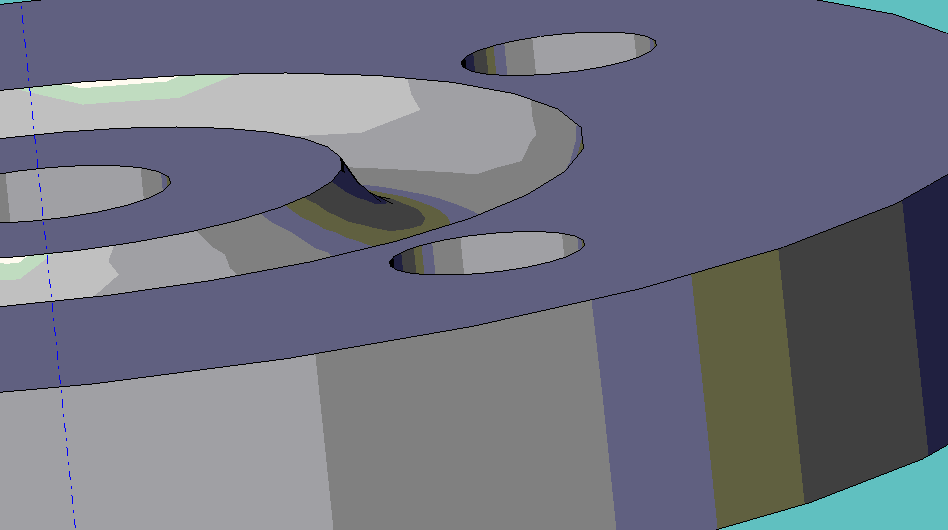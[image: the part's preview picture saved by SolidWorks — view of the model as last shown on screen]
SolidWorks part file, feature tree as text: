
SOLIDWORKS PART (.sldprt)
format: sldprt  version: not decoded by parser v0  size: 194,560 bytes
history: native  units: mm
features: sketch x4, cut_extrude x2, material x1, extrude x1, cut_revolve x1 (+12 scaffold rows collapsed)
feature tree (21):
  scaffold x12  (default folders/planes/origin — collapsed)
  material  "Material <not specified>"
  sketch  "Sketch1"  dims[D1=~12.69413mm]
  sketch  "Sketch3"  dims[D1=1.0033mm]
  extrude  "Extrude1"  Depth=3.175mm
  cut_revolve  "Cut-Revolve1"  Angle=360deg
  cut_extrude  "Cut-Extrude1"  [1 undecoded]
  sketch  "Sketch1<3>"  dims[D1=3.175mm]
  cut_extrude  "Cut-Extrude2"  [1 undecoded]
  sketch  "Sketch1<4>"  dims[D1=3.175mm]
decode coverage: 6 of 8 modeling features carry decoded parameters
note: ~ marks probable driven/reference dimensions
note: 2 parameter values undecoded
note: suppression state not decoded; provenance and decode notes live in map.json
